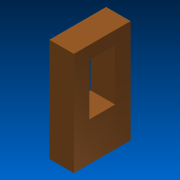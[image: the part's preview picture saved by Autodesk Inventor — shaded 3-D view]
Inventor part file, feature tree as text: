
AUTODESK INVENTOR PART (.ipt)
format: ipt  version: 2011 SP1 (Build 150282100, 282)  size: 84,992 bytes
history: native  units: mm
features: extrude x2, sketch x2, reference x1
ambient origin geometry x8: Origin, YZ Plane, XZ Plane, XY Plane, X Axis, Y Axis, Z Axis, Center Point
bodies: Solid1 (feature_tree)
feature tree (5):
  extrude  "Extrusion1"  Depth=2.2mm
  extrude  "Extrusion2"  Depth=1.0mm
  sketch  "Sketch1"  dims[d0=0.95mm d1=2.2mm]
  reference  "Reference1"
  sketch  "Sketch2"  dims[d2=4.0mm d3=0.0mm d4=1.0mm d5=2.0mm d6=0.5mm d7=4.0mm d8=0.0mm]
